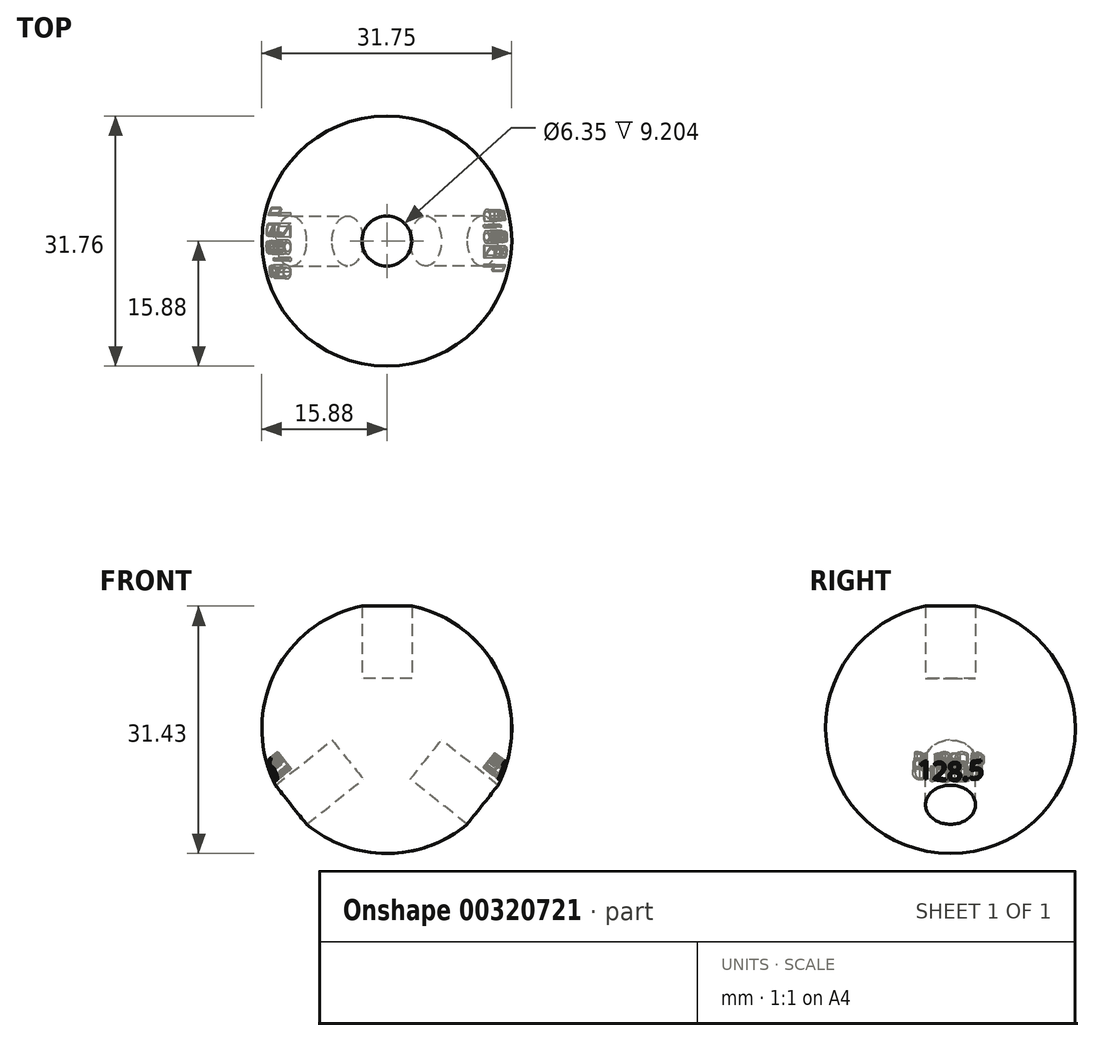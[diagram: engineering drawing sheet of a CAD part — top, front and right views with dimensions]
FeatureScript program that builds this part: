
annotation { "Feature Type Name" : "Feature", "Feature Type Description" : "" }
export const myFeature = defineFeature(function(context is Context, id is Id, definition is map)
    precondition{}
    {
        {
            var Q0;
            Q0=qCreatedBy(makeId("Front.planeOp"),FACE);
            var sketch = newSketch(context, id + "F0", { "sketchPlane" : qUnion([Q0])});
            skArc(sketch, "E0", {"start": v(0, 15.88) * mm, "mid": v(-15.88, 0) * mm, "end": v(0, -15.88) * mm});
            skLineSegment(sketch, "E1", {"start": v(0, 15.88) * mm, "end": v(0, -15.88) * mm});
            skSolve(sketch);
        }
        {
            var Q0;
            Q0=qCreatedBy(makeId("Top.planeOp"),FACE);
            var sketch = newSketch(context, id + "F1", { "sketchPlane" : qUnion([Q0])});
            skCircle(sketch, "E2", {"center": v(0, 0) * mm, "radius": 15.88 * mm});
            skSolve(sketch);
        }
        {
            var Q0;
            Q0=makeQuery(id+"F0.imprint","IMPRINT",FACE,{"disambiguationData":[TD([[makeQuery(id+"F0.imprint","IMPRINT",EDGE,{"derivedFrom":sQuery(id+"F0.wireOp",EDGE,"E0")}),1.0]])]});
            var Q1;
            Q1=sQuery(id+"F1.wireOp",EDGE,"E2");
            revolve(context, id + "F2", {"entities" : qUnion([Q0]), "axis" : qUnion([Q1]), "revolveType" : RevolveType.FULL});
        }
        {
            var Q0;
            Q0=qCreatedBy(makeId("Top.planeOp"),FACE);
            cPlane(context, id + "F3", {"entities" : qUnion([Q0]), "cplaneType" : CPlaneType.OFFSET, "offset" : 6.35 * mm, "width" : 152.4 * mm, "height" : 152.4 * mm});
        }
        {
            var Q0;
            Q0=qCreatedBy(id+"F3.planeOp",FACE);
            var sketch = newSketch(context, id + "F4", { "sketchPlane" : qUnion([Q0])});
            skCircle(sketch, "E3", {"center": v(0, 0) * mm, "radius": 3.18 * mm});
            skSolve(sketch);
        }
        {
            var Q0;
            Q0=makeQuery(id+"F4.imprint","IMPRINT",FACE,{"disambiguationData":[TD([[makeQuery(id+"F4.imprint","IMPRINT",EDGE,{"derivedFrom":sQuery(id+"F4.wireOp",EDGE,"E3")}),1.0]])]});
            extrude(context, id + "F5", {"entities" : qUnion([Q0]), "depth" : 50.8 * mm});
        }
        {
            var Q0;
            Q0=qCreatedBy(makeId("Right.planeOp"),FACE);
            var sketch = newSketch(context, id + "F6", { "sketchPlane" : qUnion([Q0])});
            skLineSegment(sketch, "E4", {"start": v(0, 0) * mm, "end": v(44.8, 0) * mm, "construction": true});
            skSolve(sketch);
        }
        {
            var Q0;
            Q0=makeQuery(id+"F5.opExtrude","SWEPT_BODY",BODY,{"disambiguationData":[OSD([sQuery(id+"F4.wireOp",EDGE,"E3")])]});
            var Q1;
            Q1=sQuery(id+"F6.wireOp",EDGE,"E4");
            transform(context, id + "F7", {"entities" : qUnion([Q0]), "transformType" : TransformType.ROTATION, "transformAxis" : qUnion([Q1]), "angle" : 128.5 * degree, "makeCopy" : true});
        }
        {
            var Q0;
            Q0=makeQuery(id+"F5.opExtrude","SWEPT_BODY",BODY,{"disambiguationData":[OSD([sQuery(id+"F4.wireOp",EDGE,"E3")])]});
            var Q1;
            Q1=sQuery(id+"F6.wireOp",EDGE,"E4");
            transform(context, id + "F8", {"entities" : qUnion([Q0]), "transformType" : TransformType.ROTATION, "transformAxis" : qUnion([Q1]), "angle" : 128.6 * degree, "oppositeDirection" : true, "makeCopy" : true});
        }
        {
            var Q0;
            Q0=makeQuery(id+"F7.opPattern","COPY",FACE,{"derivedFrom":makeQuery(id+"F5.opExtrude","CAP_FACE",FACE,{"disambiguationData":[OSD([sQuery(id+"F4.wireOp",EDGE,"E3")])],"isStart":false}),"instanceName":"1"});
            cPlane(context, id + "F9", {"entities" : qUnion([Q0]), "cplaneType" : CPlaneType.OFFSET, "offset" : 38.1 * mm, "oppositeDirection" : true, "width" : 152.4 * mm, "height" : 152.4 * mm});
        }
        {
            var Q0;
            Q0=qCreatedBy(id+"F9.planeOp",FACE);
            var sketch = newSketch(context, id + "F10", { "sketchPlane" : qUnion([Q0])});
            skText(sketch, "E5", { "text": "128.5\n", "fontName": "OpenSans-Regular.ttf"});
            const initialGuessF10  = {"E5": [-0.00413, 0.0038, 1, 0, 0.00235]};
            skSetInitialGuess(sketch, initialGuessF10);
            skSolve(sketch);
        }
        {
            var Q0;
            Q0=qSketchRegion(id+"F10",true);
            extrude(context, id + "F11", {"entities" : qUnion([Q0]), "operationType" : NewBodyOperationType.REMOVE, "oppositeDirection" : true, "depth" : 6.35 * mm});
        }
        {
            var Q0;
            Q0=makeQuery(id+"F8.opPattern","COPY",FACE,{"derivedFrom":makeQuery(id+"F5.opExtrude","CAP_FACE",FACE,{"disambiguationData":[OSD([sQuery(id+"F4.wireOp",EDGE,"E3")])],"isStart":false}),"instanceName":"1"});
            cPlane(context, id + "F12", {"entities" : qUnion([Q0]), "cplaneType" : CPlaneType.OFFSET, "offset" : 38.1 * mm, "oppositeDirection" : true, "width" : 152.4 * mm, "height" : 152.4 * mm});
        }
        {
            var Q0;
            Q0=qCreatedBy(id+"F12.planeOp",FACE);
            var sketch = newSketch(context, id + "F13", { "sketchPlane" : qUnion([Q0])});
            skText(sketch, "E6", { "text": "128.6\n", "fontName": "OpenSans-Regular.ttf"});
            const initialGuessF13  = {"E6": [-0.00456, 0.0036, 1, 0, 0.00269]};
            skSetInitialGuess(sketch, initialGuessF13);
            skSolve(sketch);
        }
        {
            var Q0;
            Q0=qSketchRegion(id+"F13",true);
            extrude(context, id + "F14", {"entities" : qUnion([Q0]), "operationType" : NewBodyOperationType.REMOVE, "oppositeDirection" : true, "depth" : 6.35 * mm});
        }
        {
            var Q0;
            Q0=makeQuery(id+"F5.opExtrude","SWEPT_BODY",BODY,{"disambiguationData":[OSD([sQuery(id+"F4.wireOp",EDGE,"E3")])]});
            var Q1;
            Q1=makeQuery(id+"F7.opPattern","COPY",BODY,{"derivedFrom":makeQuery(id+"F5.opExtrude","SWEPT_BODY",BODY,{"disambiguationData":[OSD([sQuery(id+"F4.wireOp",EDGE,"E3")])]}),"instanceName":"1"});
            var Q2;
            Q2=makeQuery(id+"F8.opPattern","COPY",BODY,{"derivedFrom":makeQuery(id+"F5.opExtrude","SWEPT_BODY",BODY,{"disambiguationData":[OSD([sQuery(id+"F4.wireOp",EDGE,"E3")])]}),"instanceName":"1"});
            var Q3;
            Q3=makeQuery(id+"F2.opRevolve","SWEPT_BODY",BODY,{"disambiguationData":[OSD([sQuery(id+"F0.wireOp",EDGE,"E0"),sQuery(id+"F0.wireOp",EDGE,"E1")])]});
            booleanBodies(context, id + "F15", {"operationType" : BooleanOperationType.SUBTRACTION, "tools" : qUnion([Q0, Q1, Q2]), "targets" : qUnion([Q3])});
        }
    });
